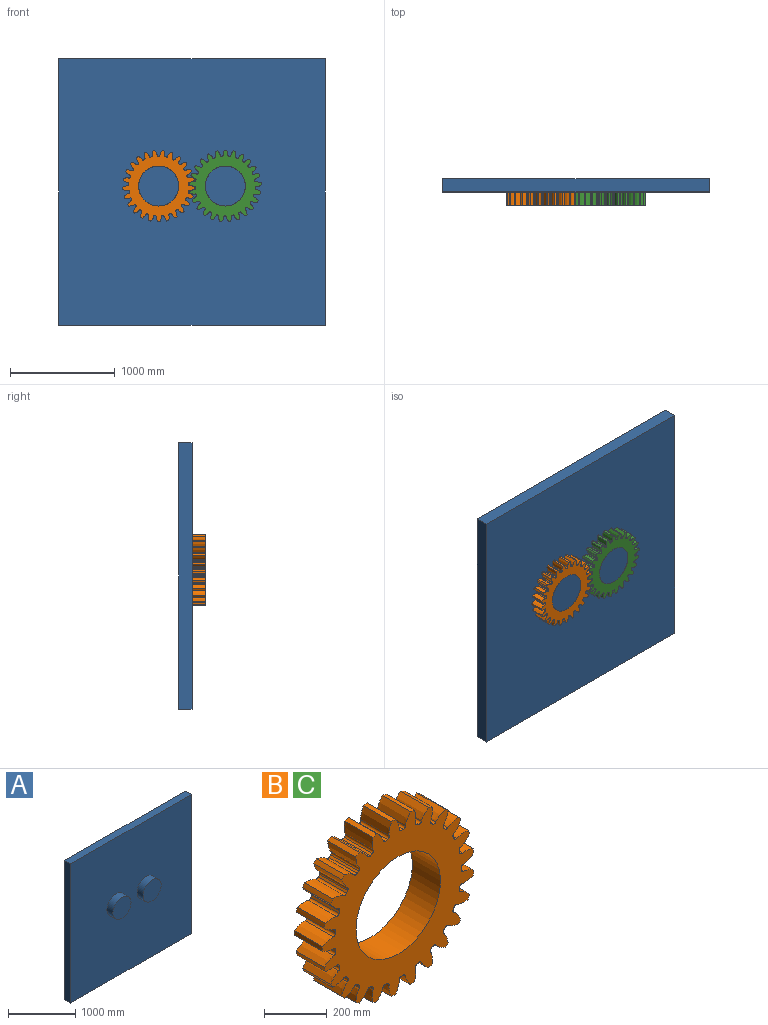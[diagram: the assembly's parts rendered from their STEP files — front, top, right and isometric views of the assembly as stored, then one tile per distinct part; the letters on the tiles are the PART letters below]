
ASSEMBLY  parts=3 mates=2
PART A: 10 faces, bbox 2540x254x2540 mm
  f0: plane 2540x127mm, normal (0,0,-1), area 322580mm2, adj f1,f3,f4,f5
  f1: plane 2540x127mm, normal (1,0,0), area 322580mm2, adj f0,f2,f4,f5
  f2: plane 2540x127mm, normal (0,0,1), area 322580mm2, adj f1,f3,f4,f5
  f3: plane 2540x127mm, normal (-1,0,0), area 322580mm2, adj f0,f2,f4,f5
  f4: plane 2540x2540mm, normal (0,-1,0), area 6223581.6mm2, adj f0,f1,f2,f3,f6,f8
  f5: plane 2540x2540mm, normal (0,1,0), area 6451600mm2, adj f0,f1,f2,f3
  f6: cylinder r=190.5mm len=381mm, axis (0,-1,0), area 152012.2mm2, adj f4,f7
  f7: plane 381x381mm, normal (0,-1,0), area 114009.2mm2, adj f6
  f8: cylinder r=190.5mm len=381mm, axis (0,-1,0), area 152012.2mm2, adj f4,f9
  f9: plane 381x381mm, normal (0,-1,0), area 114009.2mm2, adj f8
PART B: 153 faces, bbox 684.2x127x685.5 mm
  f0: extruded ~127x46.83mm, area 6540.1mm2, adj f100,f101,f102,f103
  f1: cylinder r=285.75mm len=127mm, axis (0,1,0), area 1225.1mm2, adj f101,f102,f103,f104
  f2: extruded ~127x46.83mm, area 6540.1mm2, adj f3,f101,f102,f104
  f3: cylinder r=342.9mm len=127mm, axis (0,1,0), area 2317.9mm2, adj f2,f4,f101,f102
  f4: extruded ~127x50.29mm, area 6540.1mm2, adj f3,f101,f102,f105
  f5: cylinder r=285.75mm len=127mm, axis (0,1,0), area 1225.1mm2, adj f101,f102,f105,f106
  f6: extruded ~127x40.43mm, area 6540.1mm2, adj f7,f101,f102,f106
  f7: cylinder r=342.9mm len=127mm, axis (0,1,0), area 2317.9mm2, adj f6,f8,f101,f102
  f8: extruded ~127x50.59mm, area 6540.1mm2, adj f7,f101,f102,f107
  f9: cylinder r=285.75mm len=127mm, axis (0,1,0), area 1225.1mm2, adj f101,f102,f107,f108
  f10: extruded ~127x39.93mm, area 6540.1mm2, adj f11,f101,f102,f108
  f11: cylinder r=342.9mm len=127mm, axis (0,1,0), area 2317.9mm2, adj f10,f12,f101,f102
  f12: extruded ~127x47.7mm, area 6540.1mm2, adj f11,f101,f102,f109
  f13: cylinder r=285.75mm len=127mm, axis (0,1,0), area 1225.1mm2, adj f101,f102,f109,f110
  f14: extruded ~127x46.5mm, area 6540.1mm2, adj f15,f101,f102,f110
  f15: cylinder r=342.9mm len=127mm, axis (0,1,0), area 2317.9mm2, adj f14,f16,f101,f102
  f16: extruded ~127x41.82mm, area 6540.1mm2, adj f15,f101,f102,f111
  f17: cylinder r=285.75mm len=127mm, axis (0,1,0), area 1225.1mm2, adj f101,f102,f111,f112
  f18: extruded ~127x50.16mm, area 6540.1mm2, adj f19,f101,f102,f112
  f19: cylinder r=342.9mm len=127mm, axis (0,1,0), area 2317.9mm2, adj f18,f20,f101,f102
  f20: extruded ~127x38.42mm, area 6540.1mm2, adj f19,f101,f102,f113
  f21: cylinder r=285.75mm len=127mm, axis (0,1,0), area 1225.1mm2, adj f101,f102,f113,f114
  f22: extruded ~127x50.66mm, area 6540.1mm2, adj f23,f101,f102,f114
  f23: cylinder r=342.9mm len=127mm, axis (0,1,0), area 2317.9mm2, adj f22,f24,f101,f102
  f24: extruded ~127x45.49mm, area 6540.1mm2, adj f23,f101,f102,f115
  f25: cylinder r=285.75mm len=127mm, axis (0,1,0), area 1225.1mm2, adj f101,f102,f115,f116
  f26: extruded ~127x47.98mm, area 6540.1mm2, adj f27,f101,f102,f116
  f27: cylinder r=342.9mm len=127mm, axis (0,1,0), area 2317.9mm2, adj f26,f28,f101,f102
  f28: extruded ~127x49.72mm, area 6540.1mm2, adj f27,f101,f102,f117
  f29: cylinder r=285.75mm len=127mm, axis (0,1,0), area 1225.1mm2, adj f101,f102,f117,f118
  f30: extruded ~127x42.29mm, area 6540.1mm2, adj f31,f101,f102,f118
  f31: cylinder r=342.9mm len=127mm, axis (0,1,0), area 2317.9mm2, adj f30,f32,f101,f102
  f32: extruded ~127x50.81mm, area 6540.1mm2, adj f31,f101,f102,f119
  f33: cylinder r=285.75mm len=127mm, axis (0,1,0), area 1225.1mm2, adj f101,f102,f119,f120
  f34: extruded ~127x37.87mm, area 6540.1mm2, adj f35,f101,f102,f120
  f35: cylinder r=342.9mm len=127mm, axis (0,1,0), area 2317.9mm2, adj f34,f36,f101,f102
  f36: extruded ~127x48.72mm, area 6540.1mm2, adj f35,f101,f102,f121
  f37: cylinder r=285.75mm len=127mm, axis (0,1,0), area 1225.1mm2, adj f101,f102,f121,f122
  f38: extruded ~127x45.12mm, area 6540.1mm2, adj f39,f101,f102,f122
  f39: cylinder r=342.9mm len=127mm, axis (0,1,0), area 2317.9mm2, adj f38,f40,f101,f102
  f40: extruded ~127x43.56mm, area 6540.1mm2, adj f39,f101,f102,f123
  f41: cylinder r=285.75mm len=127mm, axis (0,1,0), area 1225.1mm2, adj f101,f102,f123,f124
  f42: extruded ~127x49.54mm, area 6540.1mm2, adj f43,f101,f102,f124
  f43: cylinder r=342.9mm len=127mm, axis (0,1,0), area 2317.9mm2, adj f42,f44,f101,f102
  f44: extruded ~127x36.25mm, area 6540.1mm2, adj f43,f101,f102,f125
  f45: cylinder r=285.75mm len=127mm, axis (0,1,0), area 1225.1mm2, adj f101,f102,f125,f126
  f46: extruded ~127x50.84mm, area 6540.1mm2, adj f47,f101,f102,f126
  f47: cylinder r=342.9mm len=127mm, axis (0,1,0), area 2317.9mm2, adj f46,f48,f101,f102
  f48: extruded ~127x43.98mm, area 6540.1mm2, adj f47,f101,f102,f127
  f49: cylinder r=285.75mm len=127mm, axis (0,1,0), area 1225.1mm2, adj f101,f102,f127,f128
  f50: extruded ~127x48.95mm, area 6540.1mm2, adj f51,f101,f102,f128
  f51: cylinder r=342.9mm len=127mm, axis (0,1,0), area 2317.9mm2, adj f50,f52,f101,f102
  f52: extruded ~127x48.95mm, area 6540.1mm2, adj f51,f101,f102,f129
  f53: cylinder r=285.75mm len=127mm, axis (0,1,0), area 1225.1mm2, adj f101,f102,f129,f130
  f54: extruded ~127x43.98mm, area 6540.1mm2, adj f55,f101,f102,f130
  f55: cylinder r=342.9mm len=127mm, axis (0,1,0), area 2317.9mm2, adj f54,f56,f101,f102
  f56: extruded ~127x50.84mm, area 6540.1mm2, adj f55,f101,f102,f131
  f57: cylinder r=285.75mm len=127mm, axis (0,1,0), area 1225.1mm2, adj f101,f102,f131,f132
  f58: extruded ~127x36.25mm, area 6540.1mm2, adj f59,f101,f102,f132
  f59: cylinder r=342.9mm len=127mm, axis (0,1,0), area 2317.9mm2, adj f58,f60,f101,f102
  f60: extruded ~127x49.54mm, area 6540.1mm2, adj f59,f101,f102,f133
  f61: cylinder r=285.75mm len=127mm, axis (0,1,0), area 1225.1mm2, adj f101,f102,f133,f134
  f62: extruded ~127x43.56mm, area 6540.1mm2, adj f63,f101,f102,f134
  f63: cylinder r=342.9mm len=127mm, axis (0,1,0), area 2317.9mm2, adj f62,f64,f101,f102
  f64: extruded ~127x45.12mm, area 6540.1mm2, adj f63,f101,f102,f135
  f65: cylinder r=285.75mm len=127mm, axis (0,1,0), area 1225.1mm2, adj f101,f102,f135,f136
  f66: extruded ~127x48.72mm, area 6540.1mm2, adj f67,f101,f102,f136
  f67: cylinder r=342.9mm len=127mm, axis (0,1,0), area 2317.9mm2, adj f66,f68,f101,f102
  f68: extruded ~127x37.87mm, area 6540.1mm2, adj f67,f101,f102,f137
  f69: cylinder r=285.75mm len=127mm, axis (0,1,0), area 1225.1mm2, adj f101,f102,f137,f138
  f70: extruded ~127x50.81mm, area 6540.1mm2, adj f71,f101,f102,f138
  f71: cylinder r=342.9mm len=127mm, axis (0,1,0), area 2317.9mm2, adj f70,f72,f101,f102
  f72: extruded ~127x42.29mm, area 6540.1mm2, adj f71,f101,f102,f139
  f73: cylinder r=285.75mm len=127mm, axis (0,1,0), area 1225.1mm2, adj f101,f102,f139,f140
  f74: extruded ~127x49.72mm, area 6540.1mm2, adj f75,f101,f102,f140
  f75: cylinder r=342.9mm len=127mm, axis (0,1,0), area 2317.9mm2, adj f74,f76,f101,f102
  f76: extruded ~127x47.98mm, area 6540.1mm2, adj f75,f101,f102,f141
  f77: cylinder r=285.75mm len=127mm, axis (0,1,0), area 1225.1mm2, adj f101,f102,f141,f142
  f78: extruded ~127x45.49mm, area 6540.1mm2, adj f79,f101,f102,f142
  f79: cylinder r=342.9mm len=127mm, axis (0,1,0), area 2317.9mm2, adj f78,f80,f101,f102
  f80: extruded ~127x50.66mm, area 6540.1mm2, adj f79,f101,f102,f143
  f81: cylinder r=285.75mm len=127mm, axis (0,1,0), area 1225.1mm2, adj f101,f102,f143,f144
  f82: extruded ~127x38.42mm, area 6540.1mm2, adj f83,f101,f102,f144
  f83: cylinder r=342.9mm len=127mm, axis (0,1,0), area 2317.9mm2, adj f82,f84,f101,f102
  f84: extruded ~127x50.16mm, area 6540.1mm2, adj f83,f101,f102,f145
  f85: cylinder r=285.75mm len=127mm, axis (0,1,0), area 1225.1mm2, adj f101,f102,f145,f146
  f86: extruded ~127x41.82mm, area 6540.1mm2, adj f87,f101,f102,f146
  f87: cylinder r=342.9mm len=127mm, axis (0,1,0), area 2317.9mm2, adj f86,f88,f101,f102
  f88: extruded ~127x46.5mm, area 6540.1mm2, adj f87,f101,f102,f147
  f89: cylinder r=285.75mm len=127mm, axis (0,1,0), area 1225.1mm2, adj f101,f102,f147,f148
  f90: extruded ~127x47.7mm, area 6540.1mm2, adj f91,f101,f102,f148
  f91: cylinder r=342.9mm len=127mm, axis (0,1,0), area 2317.9mm2, adj f90,f92,f101,f102
  f92: extruded ~127x39.93mm, area 6540.1mm2, adj f91,f101,f102,f149
  f93: cylinder r=285.75mm len=127mm, axis (0,1,0), area 1225.1mm2, adj f101,f102,f149,f150
  f94: extruded ~127x50.59mm, area 6540.1mm2, adj f95,f101,f102,f150
  f95: cylinder r=342.9mm len=127mm, axis (0,1,0), area 2317.9mm2, adj f94,f96,f101,f102
  f96: extruded ~127x40.43mm, area 6540.1mm2, adj f95,f101,f102,f151
  f97: cylinder r=285.75mm len=127mm, axis (0,1,0), area 1225.1mm2, adj f101,f102,f151,f152
  f98: extruded ~127x50.29mm, area 6540.1mm2, adj f100,f101,f102,f152
  f99: cylinder r=190.5mm len=381mm, axis (0,1,0), area 152012.2mm2, adj f101,f102
  f100: cylinder r=342.9mm len=127mm, axis (0,1,0), area 2317.9mm2, adj f0,f98,f101,f102
  f101: plane 685.5x684.2mm, normal (0,-1,0), area 197916.5mm2, adj f0,f1,f2,f3,f4,f5,f6,f7
  f102: plane 685.5x684.2mm, normal (0,1,0), area 197916.5mm2, adj f0,f1,f2,f3,f4,f5,f6,f7
  f103: cylinder r=9.13mm len=127mm, axis (0,1,0), area 1783.5mm2, adj f0,f1,f101,f102
  f104: cylinder r=9.13mm len=127mm, axis (0,1,0), area 1783.5mm2, adj f1,f2,f101,f102
  f105: cylinder r=9.13mm len=127mm, axis (0,1,0), area 1783.5mm2, adj f4,f5,f101,f102
  f106: cylinder r=9.13mm len=127mm, axis (0,1,0), area 1783.5mm2, adj f5,f6,f101,f102
  f107: cylinder r=9.13mm len=127mm, axis (0,1,0), area 1783.5mm2, adj f8,f9,f101,f102
  f108: cylinder r=9.13mm len=127mm, axis (0,1,0), area 1783.5mm2, adj f9,f10,f101,f102
  f109: cylinder r=9.13mm len=127mm, axis (0,1,0), area 1783.5mm2, adj f12,f13,f101,f102
  f110: cylinder r=9.13mm len=127mm, axis (0,1,0), area 1783.5mm2, adj f13,f14,f101,f102
  f111: cylinder r=9.13mm len=127mm, axis (0,1,0), area 1783.5mm2, adj f16,f17,f101,f102
  f112: cylinder r=9.13mm len=127mm, axis (0,1,0), area 1783.5mm2, adj f17,f18,f101,f102
  f113: cylinder r=9.13mm len=127mm, axis (0,1,0), area 1783.5mm2, adj f20,f21,f101,f102
  f114: cylinder r=9.13mm len=127mm, axis (0,1,0), area 1783.5mm2, adj f21,f22,f101,f102
  f115: cylinder r=9.13mm len=127mm, axis (0,1,0), area 1783.5mm2, adj f24,f25,f101,f102
  f116: cylinder r=9.13mm len=127mm, axis (0,1,0), area 1783.5mm2, adj f25,f26,f101,f102
  f117: cylinder r=9.13mm len=127mm, axis (0,1,0), area 1783.5mm2, adj f28,f29,f101,f102
  f118: cylinder r=9.13mm len=127mm, axis (0,1,0), area 1783.5mm2, adj f29,f30,f101,f102
  f119: cylinder r=9.13mm len=127mm, axis (0,1,0), area 1783.5mm2, adj f32,f33,f101,f102
  f120: cylinder r=9.13mm len=127mm, axis (0,1,0), area 1783.5mm2, adj f33,f34,f101,f102
  f121: cylinder r=9.13mm len=127mm, axis (0,1,0), area 1783.5mm2, adj f36,f37,f101,f102
  f122: cylinder r=9.13mm len=127mm, axis (0,1,0), area 1783.5mm2, adj f37,f38,f101,f102
  f123: cylinder r=9.13mm len=127mm, axis (0,1,0), area 1783.5mm2, adj f40,f41,f101,f102
  f124: cylinder r=9.13mm len=127mm, axis (0,1,0), area 1783.5mm2, adj f41,f42,f101,f102
  f125: cylinder r=9.13mm len=127mm, axis (0,1,0), area 1783.5mm2, adj f44,f45,f101,f102
  f126: cylinder r=9.13mm len=127mm, axis (0,1,0), area 1783.5mm2, adj f45,f46,f101,f102
  f127: cylinder r=9.13mm len=127mm, axis (0,1,0), area 1783.5mm2, adj f48,f49,f101,f102
  f128: cylinder r=9.13mm len=127mm, axis (0,1,0), area 1783.5mm2, adj f49,f50,f101,f102
  f129: cylinder r=9.13mm len=127mm, axis (0,1,0), area 1783.5mm2, adj f52,f53,f101,f102
  f130: cylinder r=9.13mm len=127mm, axis (0,1,0), area 1783.5mm2, adj f53,f54,f101,f102
  f131: cylinder r=9.13mm len=127mm, axis (0,1,0), area 1783.5mm2, adj f56,f57,f101,f102
  f132: cylinder r=9.13mm len=127mm, axis (0,1,0), area 1783.5mm2, adj f57,f58,f101,f102
  f133: cylinder r=9.13mm len=127mm, axis (0,1,0), area 1783.5mm2, adj f60,f61,f101,f102
  f134: cylinder r=9.13mm len=127mm, axis (0,1,0), area 1783.5mm2, adj f61,f62,f101,f102
  f135: cylinder r=9.13mm len=127mm, axis (0,1,0), area 1783.5mm2, adj f64,f65,f101,f102
  f136: cylinder r=9.13mm len=127mm, axis (0,1,0), area 1783.5mm2, adj f65,f66,f101,f102
  f137: cylinder r=9.13mm len=127mm, axis (0,1,0), area 1783.5mm2, adj f68,f69,f101,f102
  f138: cylinder r=9.13mm len=127mm, axis (0,1,0), area 1783.5mm2, adj f69,f70,f101,f102
  f139: cylinder r=9.13mm len=127mm, axis (0,1,0), area 1783.5mm2, adj f72,f73,f101,f102
  f140: cylinder r=9.13mm len=127mm, axis (0,1,0), area 1783.5mm2, adj f73,f74,f101,f102
  f141: cylinder r=9.13mm len=127mm, axis (0,1,0), area 1783.5mm2, adj f76,f77,f101,f102
  f142: cylinder r=9.13mm len=127mm, axis (0,1,0), area 1783.5mm2, adj f77,f78,f101,f102
  f143: cylinder r=9.13mm len=127mm, axis (0,1,0), area 1783.5mm2, adj f80,f81,f101,f102
  f144: cylinder r=9.13mm len=127mm, axis (0,1,0), area 1783.5mm2, adj f81,f82,f101,f102
  f145: cylinder r=9.13mm len=127mm, axis (0,1,0), area 1783.5mm2, adj f84,f85,f101,f102
  f146: cylinder r=9.13mm len=127mm, axis (0,1,0), area 1783.5mm2, adj f85,f86,f101,f102
  f147: cylinder r=9.13mm len=127mm, axis (0,1,0), area 1783.5mm2, adj f88,f89,f101,f102
  f148: cylinder r=9.13mm len=127mm, axis (0,1,0), area 1783.5mm2, adj f89,f90,f101,f102
  f149: cylinder r=9.13mm len=127mm, axis (0,1,0), area 1783.5mm2, adj f92,f93,f101,f102
  f150: cylinder r=9.13mm len=127mm, axis (0,1,0), area 1783.5mm2, adj f93,f94,f101,f102
  f151: cylinder r=9.13mm len=127mm, axis (0,1,0), area 1783.5mm2, adj f96,f97,f101,f102
  f152: cylinder r=9.13mm len=127mm, axis (0,1,0), area 1783.5mm2, adj f97,f98,f101,f102
PART C: same geometry as B
PLACE A t=(-455.42,-132.44,-101.81)mm fixed
PLACE B rot(axis=(0,1,0),24.9deg) t=(-777.54,-259.44,66.36)mm
PLACE C rot(axis=(0,-1,0),24.9deg) t=(-142.54,-259.44,66.36)mm
MATE revolute B.f3 <-> A.f6  axis (0,-1,0) through (-777.54,-386.44,66.36)mm
MATE revolute C.f3 <-> A.f8  axis (0,-1,0) through (-142.54,-386.44,66.36)mm
